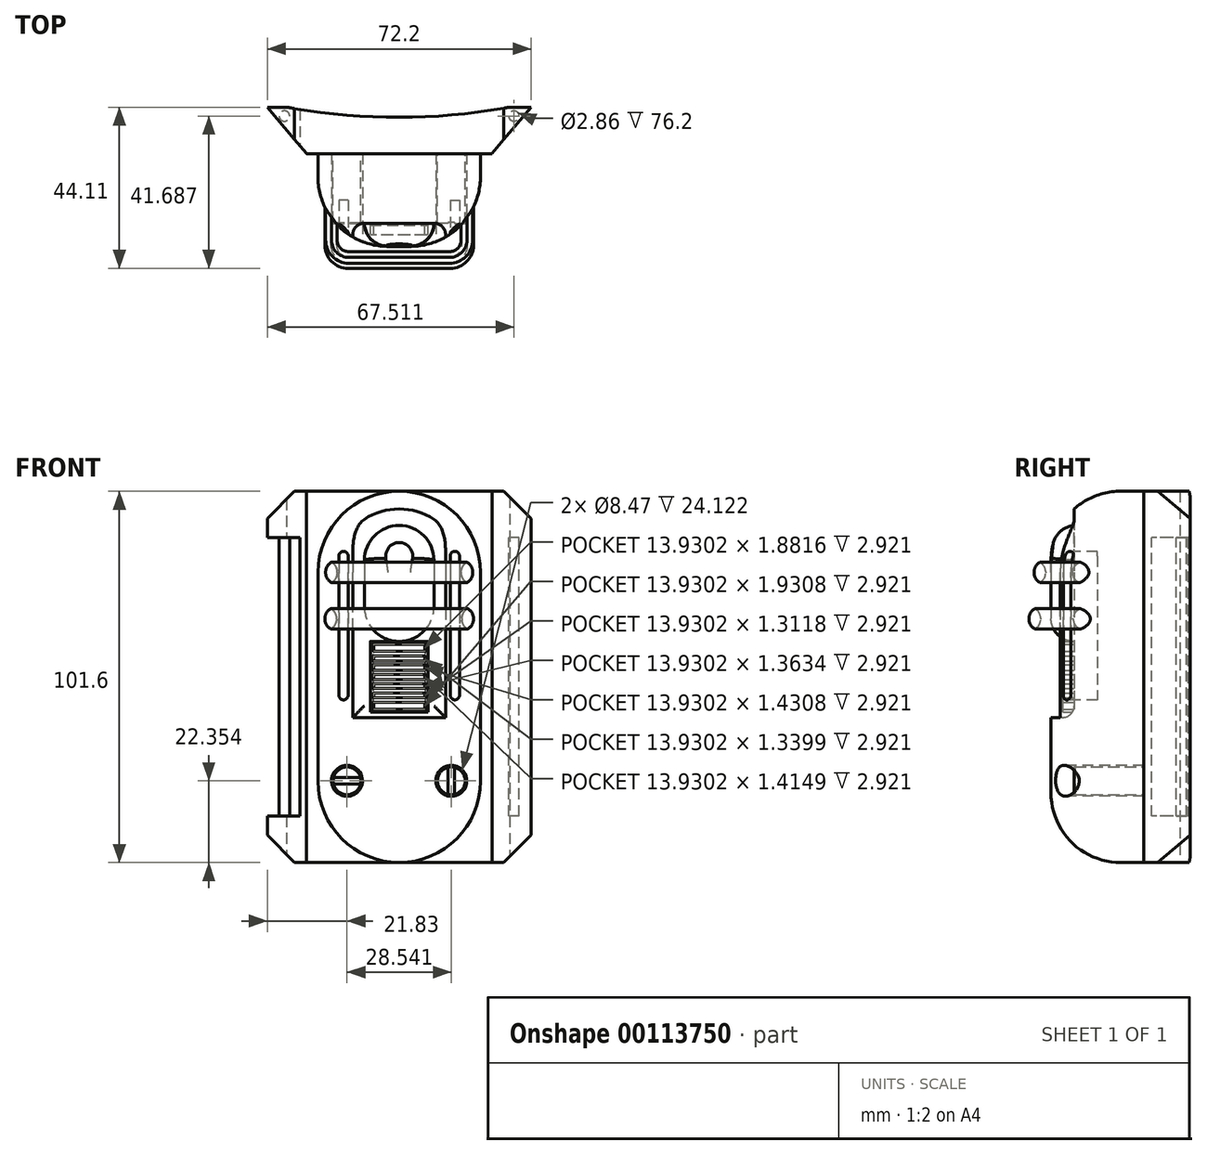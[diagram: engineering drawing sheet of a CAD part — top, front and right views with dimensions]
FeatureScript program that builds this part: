
annotation { "Feature Type Name" : "Feature", "Feature Type Description" : "" }
export const myFeature = defineFeature(function(context is Context, id is Id, definition is map)
    precondition{}
    {
        {
            var Q0;
            Q0=qCreatedBy(makeId("Front.planeOp"),FACE);
            var sketch = newSketch(context, id + "F0", { "sketchPlane" : qUnion([Q0])});
            skLineSegment(sketch, "E0.bottom", {"start": v(25.4, 50.8) * mm, "end": v(-25.4, 50.8) * mm});
            skLineSegment(sketch, "E0.top", {"start": v(25.4, -50.8) * mm, "end": v(-25.4, -50.8) * mm});
            skLineSegment(sketch, "E0.left", {"start": v(25.4, 50.8) * mm, "end": v(25.4, -50.8) * mm});
            skLineSegment(sketch, "E0.right", {"start": v(-25.4, 50.8) * mm, "end": v(-25.4, -50.8) * mm});
            skPoint(sketch, "E0.middle", {"position": v(0, 0) * mm});
            skSolve(sketch);
        }
        {
            var Q0;
            Q0 = qSketchRegion(id + "F0", true);
            extrude(context, id + "F1", {"entities" : qUnion([Q0]), "depth" : 12.7 * mm});
        }
        {
            var Q0;
            Q0=qCreatedBy(makeId("Top.planeOp"),FACE);
            var sketch = newSketch(context, id + "F2", { "sketchPlane" : qUnion([Q0])});
            skLineSegment(sketch, "E1", {"start": v(25.4, 0) * mm, "end": v(36.1, 0) * mm});
            skLineSegment(sketch, "E2", {"start": v(36.1, 0) * mm, "end": v(25.4, -12.67) * mm});
            skLineSegment(sketch, "E3", {"start": v(25.4, -12.67) * mm, "end": v(25.4, 0) * mm});
            skLineSegment(sketch, "E4.MirrorCS", {"start": v(-36.1, 0) * mm, "end": v(-25.4, -12.67) * mm});
            skLineSegment(sketch, "E5.MirrorCS", {"start": v(-25.4, -12.67) * mm, "end": v(-25.4, 0) * mm});
            skLineSegment(sketch, "E6.MirrorCS", {"start": v(-25.4, 0) * mm, "end": v(-36.1, 0) * mm});
            skSolve(sketch);
        }
        {
            var Q0;
            Q0 = qSketchRegion(id + "F2", true);
            extrude(context, id + "F3", {"entities" : qUnion([Q0]), "operationType" : NewBodyOperationType.ADD, "depth" : 101.6 * mm, "symmetric" : true});
        }
        {
            var Q0;
            Q0=qCreatedBy(makeId("Top.planeOp"),FACE);
            var sketch = newSketch(context, id + "F4", { "sketchPlane" : qUnion([Q0])});
            skCircle(sketch, "E7", {"center": v(-31.41, -2.42) * mm, "radius": 1.43 * mm});
            skCircle(sketch, "E8.MirrorC", {"center": v(31.41, -2.42) * mm, "radius": 1.43 * mm});
            skLineSegment(sketch, "E9.bottom", {"start": v(27.18, 1.43) * mm, "end": v(39.9, 1.43) * mm});
            skLineSegment(sketch, "E9.top", {"start": v(27.18, -11.19) * mm, "end": v(39.9, -11.19) * mm});
            skLineSegment(sketch, "E9.left", {"start": v(27.18, 1.43) * mm, "end": v(27.18, -11.19) * mm});
            skLineSegment(sketch, "E9.right", {"start": v(39.9, 1.43) * mm, "end": v(39.9, -11.19) * mm});
            skLineSegment(sketch, "E10.MirrorCS", {"start": v(-27.18, -11.19) * mm, "end": v(-39.9, -11.19) * mm});
            skLineSegment(sketch, "E11.MirrorCS", {"start": v(-39.9, 1.43) * mm, "end": v(-39.9, -11.19) * mm});
            skLineSegment(sketch, "E12.MirrorCS", {"start": v(-27.18, 1.43) * mm, "end": v(-39.9, 1.43) * mm});
            skLineSegment(sketch, "E13.MirrorCS", {"start": v(-27.18, 1.43) * mm, "end": v(-27.18, -11.19) * mm});
            skSolve(sketch);
        }
        {
            var Q0;
            Q0=makeQuery(id+"F4.imprint","IMPRINT",FACE,{"disambiguationData":[TD([[makeQuery(id+"F4.imprint","IMPRINT",EDGE,{"derivedFrom":sQuery(id+"F4.wireOp",EDGE,"E8.MirrorC")}),1.0]])]});
            var Q1;
            Q1=makeQuery(id+"F4.imprint","IMPRINT",FACE,{"disambiguationData":[TD([[makeQuery(id+"F4.imprint","IMPRINT",EDGE,{"derivedFrom":sQuery(id+"F4.wireOp",EDGE,"E7")}),-1.0]])]});
            extrude(context, id + "F5", {"entities" : qUnion([Q0, Q1]), "operationType" : NewBodyOperationType.REMOVE, "oppositeDirection" : true, "depth" : 76.2 * mm, "symmetric" : true});
        }
        {
            var Q0;
            Q0=qCreatedBy(makeId("Front.planeOp"),FACE);
            var sketch = newSketch(context, id + "F6", { "sketchPlane" : qUnion([Q0])});
            skLineSegment(sketch, "E14", {"start": v(-40.53, 38.9) * mm, "end": v(-23.28, 56.16) * mm});
            skLineSegment(sketch, "E15", {"start": v(-23.28, 56.16) * mm, "end": v(-40.53, 56.16) * mm});
            skLineSegment(sketch, "E16", {"start": v(-40.53, 56.16) * mm, "end": v(-40.53, 38.9) * mm});
            skLineSegment(sketch, "E17.MirrorCS", {"start": v(40.53, 56.16) * mm, "end": v(40.53, 38.9) * mm});
            skLineSegment(sketch, "E18.MirrorCS", {"start": v(23.28, 56.16) * mm, "end": v(40.53, 56.16) * mm});
            skLineSegment(sketch, "E19.MirrorCS", {"start": v(40.53, 38.9) * mm, "end": v(23.28, 56.16) * mm});
            skLineSegment(sketch, "E20.MirrorCS", {"start": v(-40.53, -56.16) * mm, "end": v(-40.53, -38.9) * mm});
            skLineSegment(sketch, "E21.MirrorCS", {"start": v(-23.28, -56.16) * mm, "end": v(-40.53, -56.16) * mm});
            skLineSegment(sketch, "E22.MirrorCS", {"start": v(-40.53, -38.9) * mm, "end": v(-23.28, -56.16) * mm});
            skLineSegment(sketch, "E23.MirrorCS", {"start": v(40.53, -38.9) * mm, "end": v(23.28, -56.16) * mm});
            skLineSegment(sketch, "E24.MirrorCS", {"start": v(23.28, -56.16) * mm, "end": v(40.53, -56.16) * mm});
            skLineSegment(sketch, "E25.MirrorCS", {"start": v(40.53, -56.16) * mm, "end": v(40.53, -38.9) * mm});
            skSolve(sketch);
        }
        {
            var Q0;
            Q0=makeQuery(id+"F6.imprint","IMPRINT",FACE,{"disambiguationData":[TD([[makeQuery(id+"F6.imprint","IMPRINT",EDGE,{"derivedFrom":sQuery(id+"F6.wireOp",EDGE,"E17.MirrorCS")}),-1.0]])]});
            var Q1;
            Q1=makeQuery(id+"F6.imprint","IMPRINT",FACE,{"disambiguationData":[TD([[makeQuery(id+"F6.imprint","IMPRINT",EDGE,{"derivedFrom":sQuery(id+"F6.wireOp",EDGE,"E20.MirrorCS")}),-1.0]])]});
            var Q2;
            Q2=makeQuery(id+"F6.imprint","IMPRINT",FACE,{"disambiguationData":[TD([[makeQuery(id+"F6.imprint","IMPRINT",EDGE,{"derivedFrom":sQuery(id+"F6.wireOp",EDGE,"E23.MirrorCS")}),1.0]])]});
            var Q3;
            Q3=makeQuery(id+"F6.imprint","IMPRINT",FACE,{"disambiguationData":[TD([[makeQuery(id+"F6.imprint","IMPRINT",EDGE,{"derivedFrom":sQuery(id+"F6.wireOp",EDGE,"E14")}),1.0]])]});
            extrude(context, id + "F7", {"entities" : qUnion([Q0, Q1, Q2, Q3]), "operationType" : NewBodyOperationType.REMOVE, "endBound" : BoundingType.THROUGH_ALL, "depth" : 25.4 * mm});
        }
        {
            var Q0;
            Q0=makeQuery(id+"F1.opExtrude","CAP_FACE",FACE,{"disambiguationData":[OSD([sQuery(id+"F0.wireOp",EDGE,"E0.bottom"),sQuery(id+"F0.wireOp",EDGE,"E0.top"),sQuery(id+"F0.wireOp",EDGE,"E0.left"),sQuery(id+"F0.wireOp",EDGE,"E0.right")])],"isStart":false});
            var sketch = newSketch(context, id + "F8", { "sketchPlane" : qUnion([Q0])});
            skLineSegment(sketch, "E26.bottom", {"start": v(22.23, 28.57) * mm, "end": v(-22.22, 28.57) * mm});
            skLineSegment(sketch, "E26.top", {"start": v(22.22, -28.58) * mm, "end": v(-22.22, -28.58) * mm});
            skLineSegment(sketch, "E26.left", {"start": v(22.22, 28.57) * mm, "end": v(22.22, -28.58) * mm});
            skLineSegment(sketch, "E26.right", {"start": v(-22.23, 28.57) * mm, "end": v(-22.23, -28.58) * mm});
            skPoint(sketch, "E26.middle", {"position": v(0, 0) * mm});
            skArc(sketch, "E27", {"start": v(22.23, 28.58) * mm, "mid": v(0, 50.8) * mm, "end": v(-22.23, 28.57) * mm});
            skArc(sketch, "E28", {"start": v(-22.23, -28.58) * mm, "mid": v(0, -50.8) * mm, "end": v(22.23, -28.58) * mm});
            skSolve(sketch);
        }
        {
            var Q0;
            Q0 = qSketchRegion(id + "F8", true);
            extrude(context, id + "F9", {"entities" : qUnion([Q0]), "operationType" : NewBodyOperationType.ADD, "depth" : 25.4 * mm});
        }
        {
            var Q0;
            Q0=makeQuery(id+"F9.opExtrude","CAP_EDGE",EDGE,{"disambiguationData":[OSD([sQuery(id+"F8.wireOp",EDGE,"E26.left")])],"isStart":false});
            fillet(context, id + "F10", {"entities" : qUnion([Q0]), "radius" : 19.05 * mm, "tangentPropagation" : true, "allowEdgeOverflow" : false});
        }
        {
            var Q0;
            Q0=makeQuery(id+"F9.opExtrude","CAP_FACE",FACE,{"disambiguationData":[OSD([sQuery(id+"F8.wireOp",EDGE,"E26.left"),sQuery(id+"F8.wireOp",EDGE,"E26.right"),sQuery(id+"F8.wireOp",EDGE,"E27"),sQuery(id+"F8.wireOp",EDGE,"E28")])],"isStart":false});
            var sketch = newSketch(context, id + "F11", { "sketchPlane" : qUnion([Q0])});
            skLineSegment(sketch, "E29.left", {"start": v(12.7, 103.58) * mm, "end": v(12.7, 7.15) * mm});
            skLineSegment(sketch, "E29.right", {"start": v(-12.7, 103.58) * mm, "end": v(-12.7, 7.15) * mm});
            skPoint(sketch, "E30.middle", {"position": v(0, 31.75) * mm});
            skLineSegment(sketch, "E31", {"start": v(-12.7, 103.58) * mm, "end": v(12.7, 103.58) * mm});
            skPoint(sketch, "E32.orphan", {"position": v(-12.7, 56.35) * mm});
            skPoint(sketch, "E33.orphan", {"position": v(12.7, 56.35) * mm});
            skLineSegment(sketch, "E34.bottom", {"start": v(9.52, 31.92) * mm, "end": v(-9.52, 31.92) * mm});
            skLineSegment(sketch, "E34.top", {"start": v(9.52, 19.22) * mm, "end": v(-9.52, 19.22) * mm});
            skLineSegment(sketch, "E34.left", {"start": v(9.52, 31.92) * mm, "end": v(9.52, 19.22) * mm});
            skLineSegment(sketch, "E34.right", {"start": v(-9.52, 31.92) * mm, "end": v(-9.52, 19.22) * mm});
            skPoint(sketch, "E34.middle", {"position": v(0, 25.57) * mm});
            skArc(sketch, "E35", {"start": v(-9.52, 19.22) * mm, "mid": v(0, 9.7) * mm, "end": v(9.52, 19.22) * mm});
            skArc(sketch, "E36", {"start": v(9.52, 31.92) * mm, "mid": v(0, 41.44) * mm, "end": v(-9.52, 31.92) * mm});
            skLineSegment(sketch, "E37.top", {"start": v(-12.7, -11.11) * mm, "end": v(12.7, -11.11) * mm});
            skLineSegment(sketch, "E37.left", {"start": v(-12.7, 7.15) * mm, "end": v(-12.7, -11.11) * mm});
            skLineSegment(sketch, "E37.right", {"start": v(12.7, 7.15) * mm, "end": v(12.7, -11.11) * mm});
            skSolve(sketch);
        }
        {
            var Q0;
            Q0 = qSketchRegion(id + "F11", true);
            extrude(context, id + "F12", {"entities" : qUnion([Q0]), "operationType" : NewBodyOperationType.REMOVE, "oppositeDirection" : true, "depth" : 6.35 * mm});
        }
        {
            var Q0;
            Q0=makeQuery(id+"F12.boolean.opBoolean","INTERSECT",EDGE,{"derivedFrom":[makeQuery(id+"F10.opFillet","BLEND_FACE",FACE,{"disambiguationData":[OSD([sQuery(id+"F8.wireOp",EDGE,"E26.right")])]}),makeQuery(id+"F12.opExtrude","SWEPT_FACE",FACE,{"disambiguationData":[OSD([sQuery(id+"F11.wireOp",EDGE,"E34.right")])]})]});
            fillet(context, id + "F13", {"entities" : qUnion([Q0]), "radius" : 6.35 * mm, "tangentPropagation" : true, "allowEdgeOverflow" : false});
        }
        {
            var Q0;
            {var subQ0=sQuery(id+"F8.wireOp",EDGE,"E26.left");var subQ1=sQuery(id+"F8.wireOp",EDGE,"E26.right");var subQ2=sQuery(id+"F8.wireOp",EDGE,"E28");Q0=makeQuery(id+"F12.boolean.opBoolean","SPLIT",FACE,{"disambiguationData":[TD([makeQuery(id+"F10.opFillet","BLEND_FACE",FACE,{"disambiguationData":[OSD([subQ2])]})])],"derivedFrom":makeQuery(id+"F9.opExtrude","CAP_FACE",FACE,{"disambiguationData":[OSD([subQ0,subQ1,sQuery(id+"F8.wireOp",EDGE,"E27"),subQ2])],"isStart":false})});}
            var sketch = newSketch(context, id + "F14", { "sketchPlane" : qUnion([Q0])});
            skCircle(sketch, "E38", {"center": v(-14.27, -28.45) * mm, "radius": 4.23 * mm});
            skCircle(sketch, "E39.MirrorC", {"center": v(14.27, -28.45) * mm, "radius": 4.23 * mm});
            skSolve(sketch);
        }
        {
            var Q0;
            Q0 = qSketchRegion(id + "F14", true);
            extrude(context, id + "F15", {"entities" : qUnion([Q0]), "operationType" : NewBodyOperationType.REMOVE, "oppositeDirection" : true, "depth" : 25.4 * mm});
        }
        {
            var Q0;
            Q0=makeQuery(id+"F15.boolean.opBoolean","COPY",FACE,{"derivedFrom":makeQuery(id+"F15.opExtrude","CAP_FACE",FACE,{"disambiguationData":[OSD([sQuery(id+"F14.wireOp",EDGE,"E38")])],"isStart":false})});
            var sketch = newSketch(context, id + "F16", { "sketchPlane" : qUnion([Q0])});
            skCircle(sketch, "E40", {"center": v(-14.27, -28.45) * mm, "radius": 3.81 * mm});
            skCircle(sketch, "E41.MirrorC", {"center": v(14.27, -28.45) * mm, "radius": 3.81 * mm});
            skSolve(sketch);
        }
        {
            var Q0;
            Q0 = qSketchRegion(id + "F16", true);
            extrude(context, id + "F17", {"entities" : qUnion([Q0]), "operationType" : NewBodyOperationType.ADD, "depth" : 19.05 * mm});
        }
        {
            var Q0;
            Q0=makeQuery(id+"F17.opExtrude","CAP_FACE",FACE,{"disambiguationData":[OSD([sQuery(id+"F16.wireOp",EDGE,"E40")])],"isStart":false});
            var sketch = newSketch(context, id + "F18", { "sketchPlane" : qUnion([Q0])});
            skLineSegment(sketch, "E42.bottom", {"start": v(-17.97, -29.34) * mm, "end": v(-10.56, -29.34) * mm});
            skLineSegment(sketch, "E42.top", {"start": v(-17.98, -27.57) * mm, "end": v(-10.56, -27.57) * mm});
            skLineSegment(sketch, "E42.right", {"start": v(-10.56, -29.34) * mm, "end": v(-10.56, -29.32) * mm});
            skArc(sketch, "E43.0", {"start": v(-10.57, -29.34) * mm, "mid": v(-10.46, -28.46) * mm, "end": v(-10.56, -27.57) * mm});
            skArc(sketch, "E44.trimOffspring", {"start": v(-17.98, -27.57) * mm, "mid": v(-18.08, -28.46) * mm, "end": v(-17.97, -29.34) * mm});
            skArc(sketch, "E45.0", {"start": v(15.15, -24.74) * mm, "mid": v(14.27, -24.64) * mm, "end": v(13.4, -24.74) * mm});
            skLineSegment(sketch, "E46.left", {"start": v(15.15, -24.74) * mm, "end": v(15.15, -32.15) * mm});
            skLineSegment(sketch, "E46.right", {"start": v(13.4, -24.74) * mm, "end": v(13.4, -32.15) * mm});
            skArc(sketch, "E47.trimOffspring", {"start": v(13.4, -32.15) * mm, "mid": v(14.27, -32.26) * mm, "end": v(15.15, -32.15) * mm});
            skSolve(sketch);
        }
        {
            var Q0;
            Q0 = qSketchRegion(id + "F18", true);
            extrude(context, id + "F19", {"entities" : qUnion([Q0]), "operationType" : NewBodyOperationType.REMOVE, "oppositeDirection" : true, "depth" : 0.25 * mm});
        }
        {
            var Q0;
            {var subQ0=sQuery(id+"F8.wireOp",EDGE,"E26.left");var subQ1=sQuery(id+"F8.wireOp",EDGE,"E26.right");var subQ2=sQuery(id+"F8.wireOp",EDGE,"E28");Q0=makeQuery(id+"F12.boolean.opBoolean","SPLIT",FACE,{"disambiguationData":[TD([makeQuery(id+"F10.opFillet","BLEND_FACE",FACE,{"disambiguationData":[OSD([subQ2])]})])],"derivedFrom":makeQuery(id+"F9.opExtrude","CAP_FACE",FACE,{"disambiguationData":[OSD([subQ0,subQ1,sQuery(id+"F8.wireOp",EDGE,"E27"),subQ2])],"isStart":false})});}
            var sketch = newSketch(context, id + "F20", { "sketchPlane" : qUnion([Q0])});
            skLineSegment(sketch, "E48.left", {"start": v(-16.5, 33.08) * mm, "end": v(-16.5, -5.02) * mm});
            skLineSegment(sketch, "E48.right", {"start": v(-13.97, 33.08) * mm, "end": v(-13.97, -5.02) * mm});
            skArc(sketch, "E49", {"start": v(-13.97, 33.08) * mm, "mid": v(-15.24, 34.35) * mm, "end": v(-16.5, 33.08) * mm});
            skArc(sketch, "E50", {"start": v(-16.5, -5.02) * mm, "mid": v(-15.24, -6.3) * mm, "end": v(-13.97, -5.02) * mm});
            skLineSegment(sketch, "E51.MirrorCS", {"start": v(16.5, 33.08) * mm, "end": v(16.5, -5.02) * mm});
            skLineSegment(sketch, "E52.MirrorCS", {"start": v(13.97, 33.08) * mm, "end": v(13.97, -5.02) * mm});
            skArc(sketch, "E53.MirrorCS", {"start": v(16.5, -5.02) * mm, "mid": v(15.24, -6.3) * mm, "end": v(13.97, -5.02) * mm});
            skArc(sketch, "E54.MirrorCS", {"start": v(13.97, 33.08) * mm, "mid": v(15.24, 34.35) * mm, "end": v(16.5, 33.08) * mm});
            skSolve(sketch);
        }
        {
            var Q0;
            Q0 = qSketchRegion(id + "F20", true);
            extrude(context, id + "F21", {"entities" : qUnion([Q0]), "operationType" : NewBodyOperationType.REMOVE, "oppositeDirection" : true, "depth" : 12.7 * mm});
        }
        {
            var Q0;
            Q0=qCreatedBy(makeId("Top.planeOp"),FACE);
            cPlane(context, id + "F22", {"entities" : qUnion([Q0]), "cplaneType" : CPlaneType.OFFSET, "offset" : 28.57 * mm, "width" : 152.4 * mm, "height" : 152.4 * mm});
        }
        {
            var Q0;
            Q0=qCreatedBy(id+"F22.planeOp",FACE);
            var sketch = newSketch(context, id + "F23", { "sketchPlane" : qUnion([Q0])});
            skLineSegment(sketch, "E55.bottom", {"start": v(0, -42.73) * mm, "end": v(-13.78, -42.73) * mm});
            skLineSegment(sketch, "E55.right", {"start": v(-20.13, -36.38) * mm, "end": v(-20.13, -27.04) * mm});
            skPoint(sketch, "E55.middle", {"position": v(-1.1, -33.3) * mm});
            skLineSegment(sketch, "E56.bottom", {"start": v(0, -39.56) * mm, "end": v(-13.78, -39.56) * mm});
            skLineSegment(sketch, "E56.right", {"start": v(-16.95, -36.38) * mm, "end": v(-16.95, -27.04) * mm});
            skPoint(sketch, "E57.orphan", {"position": v(14.74, -27.04) * mm});
            skPoint(sketch, "E58.orphan", {"position": v(17.92, -23.87) * mm});
            skLineSegment(sketch, "E59.trimOffspring", {"start": v(-16.95, -27.04) * mm, "end": v(-20.13, -27.04) * mm});
            skPoint(sketch, "E60.orphan", {"position": v(-20.13, -23.87) * mm});
            skPoint(sketch, "E61.visualSharp", {"position": v(-20.13, -42.73) * mm});
            skArc(sketch, "E61.filletArc", {"start": v(-20.13, -36.38) * mm, "mid": v(-18.27, -40.87) * mm, "end": v(-13.78, -42.73) * mm});
            skPoint(sketch, "E62.visualSharp", {"position": v(-16.95, -39.56) * mm});
            skArc(sketch, "E62.filletArc", {"start": v(-16.95, -36.38) * mm, "mid": v(-16.02, -38.63) * mm, "end": v(-13.78, -39.56) * mm});
            skPoint(sketch, "E63.visualSharp", {"position": v(14.74, -39.56) * mm});
            skPoint(sketch, "E64.visualSharp", {"position": v(17.92, -42.73) * mm});
            skLineSegment(sketch, "E65.MirrorCS", {"start": v(0, -42.73) * mm, "end": v(13.78, -42.73) * mm});
            skLineSegment(sketch, "E66.MirrorCS", {"start": v(0, -39.56) * mm, "end": v(13.78, -39.56) * mm});
            skArc(sketch, "E67.MirrorCS", {"start": v(20.13, -36.38) * mm, "mid": v(18.27, -40.87) * mm, "end": v(13.78, -42.73) * mm});
            skArc(sketch, "E68.MirrorCS", {"start": v(16.95, -36.38) * mm, "mid": v(16.02, -38.63) * mm, "end": v(13.78, -39.56) * mm});
            skLineSegment(sketch, "E69.MirrorCS", {"start": v(16.95, -36.38) * mm, "end": v(16.95, -27.04) * mm});
            skLineSegment(sketch, "E70.MirrorCS", {"start": v(20.13, -36.38) * mm, "end": v(20.13, -27.04) * mm});
            skLineSegment(sketch, "E71.MirrorCS", {"start": v(16.95, -27.04) * mm, "end": v(20.13, -27.04) * mm});
            skSolve(sketch);
        }
        {
            var Q0;
            Q0=qCreatedBy(id+"F22.planeOp",FACE);
            cPlane(context, id + "F24", {"entities" : qUnion([Q0]), "cplaneType" : CPlaneType.OFFSET, "offset" : 12.7 * mm, "oppositeDirection" : true, "width" : 152.4 * mm, "height" : 152.4 * mm});
        }
        {
            var Q0;
            Q0=qCreatedBy(id+"F24.planeOp",FACE);
            var sketch = newSketch(context, id + "F25", { "sketchPlane" : qUnion([Q0])});
            skLineSegment(sketch, "E72.bottom", {"start": v(13.97, -44.11) * mm, "end": v(-13.97, -44.11) * mm});
            skLineSegment(sketch, "E72.left", {"start": v(20.32, -37.76) * mm, "end": v(20.32, -27.06) * mm});
            skLineSegment(sketch, "E72.right", {"start": v(-20.32, -37.76) * mm, "end": v(-20.32, -27.06) * mm});
            skPoint(sketch, "E72.middle", {"position": v(0, -34) * mm});
            skLineSegment(sketch, "E73.bottom", {"start": v(13.97, -40.94) * mm, "end": v(-13.97, -40.94) * mm});
            skLineSegment(sketch, "E73.top", {"start": v(20.32, -27.06) * mm, "end": v(15.84, -27.06) * mm});
            skLineSegment(sketch, "E73.left", {"start": v(17.15, -37.76) * mm, "end": v(17.15, -27.06) * mm});
            skLineSegment(sketch, "E73.right", {"start": v(-17.15, -37.76) * mm, "end": v(-17.15, -27.06) * mm});
            skPoint(sketch, "E74.orphan", {"position": v(17.15, -27.06) * mm});
            skPoint(sketch, "E75.orphan", {"position": v(20.32, -23.88) * mm});
            skLineSegment(sketch, "E76.trimOffspring", {"start": v(-17.15, -27.06) * mm, "end": v(-20.32, -27.06) * mm});
            skPoint(sketch, "E77.orphan", {"position": v(-20.32, -23.88) * mm});
            skPoint(sketch, "E78.visualSharp", {"position": v(-20.32, -44.11) * mm});
            skArc(sketch, "E78.filletArc", {"start": v(-20.32, -37.76) * mm, "mid": v(-18.46, -42.25) * mm, "end": v(-13.97, -44.11) * mm});
            skPoint(sketch, "E79.visualSharp", {"position": v(-17.15, -40.94) * mm});
            skArc(sketch, "E79.filletArc", {"start": v(-17.15, -37.76) * mm, "mid": v(-16.22, -40) * mm, "end": v(-13.97, -40.94) * mm});
            skPoint(sketch, "E80.visualSharp", {"position": v(17.15, -40.94) * mm});
            skArc(sketch, "E80.filletArc", {"start": v(13.97, -40.94) * mm, "mid": v(16.22, -40) * mm, "end": v(17.15, -37.76) * mm});
            skPoint(sketch, "E81.visualSharp", {"position": v(20.32, -44.11) * mm});
            skArc(sketch, "E81.filletArc", {"start": v(13.97, -44.11) * mm, "mid": v(18.46, -42.25) * mm, "end": v(20.32, -37.76) * mm});
            skSolve(sketch);
        }
        {
            var Q0;
            Q0 = qSketchRegion(id + "F23", true);
            extrude(context, id + "F26", {"entities" : qUnion([Q0]), "operationType" : NewBodyOperationType.ADD, "depth" : 6.35 * mm, "symmetric" : true});
        }
        {
            var Q0;
            Q0=makeQuery(id+"F26.opExtrude","CAP_EDGE",EDGE,{"disambiguationData":[OSD([sQuery(id+"F23.wireOp",EDGE,"E55.bottom")])],"isStart":true});
            var Q1;
            Q1=makeQuery(id+"F26.opExtrude","CAP_EDGE",EDGE,{"disambiguationData":[OSD([sQuery(id+"F23.wireOp",EDGE,"E55.bottom")])],"isStart":false});
            var Q2;
            Q2=makeQuery(id+"F26.opExtrude","CAP_EDGE",EDGE,{"disambiguationData":[OSD([sQuery(id+"F23.wireOp",EDGE,"E56.bottom")])],"isStart":true});
            var Q3;
            Q3=makeQuery(id+"F26.opExtrude","CAP_EDGE",EDGE,{"disambiguationData":[OSD([sQuery(id+"F23.wireOp",EDGE,"E56.bottom")])],"isStart":false});
            fillet(context, id + "F27", {"entities" : qUnion([Q0, Q1, Q2, Q3]), "radius" : 3.05 * mm, "tangentPropagation" : true, "allowEdgeOverflow" : false});
        }
        {
            var Q0;
            Q0 = qSketchRegion(id + "F25", true);
            extrude(context, id + "F28", {"entities" : qUnion([Q0]), "operationType" : NewBodyOperationType.ADD, "depth" : 6.35 * mm, "symmetric" : true});
        }
        {
            var Q0;
            Q0=makeQuery(id+"F28.opExtrude","CAP_EDGE",EDGE,{"disambiguationData":[OSD([sQuery(id+"F25.wireOp",EDGE,"E72.bottom")])],"isStart":false});
            var Q1;
            Q1=makeQuery(id+"F28.opExtrude","CAP_EDGE",EDGE,{"disambiguationData":[OSD([sQuery(id+"F25.wireOp",EDGE,"E73.bottom")])],"isStart":false});
            var Q2;
            Q2=makeQuery(id+"F28.opExtrude","CAP_EDGE",EDGE,{"disambiguationData":[OSD([sQuery(id+"F25.wireOp",EDGE,"E72.bottom")])],"isStart":true});
            var Q3;
            Q3=makeQuery(id+"F28.opExtrude","CAP_EDGE",EDGE,{"disambiguationData":[OSD([sQuery(id+"F25.wireOp",EDGE,"E73.bottom")])],"isStart":true});
            fillet(context, id + "F29", {"entities" : qUnion([Q0, Q1, Q2, Q3]), "radius" : 3.05 * mm, "tangentPropagation" : true, "allowEdgeOverflow" : false});
        }
        {
            var Q0;
            Q0=makeQuery(id+"F12.boolean.opBoolean","COPY",FACE,{"derivedFrom":makeQuery(id+"F12.opExtrude","CAP_FACE",FACE,{"disambiguationData":[OSD([sQuery(id+"F11.wireOp",EDGE,"E29.left"),sQuery(id+"F11.wireOp",EDGE,"E29.right"),sQuery(id+"F11.wireOp",EDGE,"E31"),sQuery(id+"F11.wireOp",EDGE,"E34.left"),sQuery(id+"F11.wireOp",EDGE,"E34.right"),sQuery(id+"F11.wireOp",EDGE,"E35"),sQuery(id+"F11.wireOp",EDGE,"E36"),sQuery(id+"F11.wireOp",EDGE,"E37.top"),sQuery(id+"F11.wireOp",EDGE,"E37.left"),sQuery(id+"F11.wireOp",EDGE,"E37.right")])],"isStart":false})});
            var sketch = newSketch(context, id + "F30", { "sketchPlane" : qUnion([Q0])});
            skLineSegment(sketch, "E82.bottom", {"start": v(6.97, 8.9) * mm, "end": v(-6.97, 8.9) * mm});
            skLineSegment(sketch, "E82.top", {"start": v(6.97, -8.9) * mm, "end": v(-6.97, -8.9) * mm});
            skLineSegment(sketch, "E82.left", {"start": v(6.97, 8.9) * mm, "end": v(6.97, 7) * mm});
            skLineSegment(sketch, "E82.right", {"start": v(-6.97, 8.9) * mm, "end": v(-6.97, 7) * mm});
            skPoint(sketch, "E82.middle", {"position": v(0, 0) * mm});
            skPoint(sketch, "E83.orphan", {"position": v(-6.97, 0) * mm});
            skPoint(sketch, "E84.start.orphan", {"position": v(6.97, 0) * mm});
            skLineSegment(sketch, "E85.bottom", {"start": v(7.88, 9.69) * mm, "end": v(-7.88, 9.69) * mm});
            skLineSegment(sketch, "E85.top", {"start": v(7.88, -9.69) * mm, "end": v(-7.88, -9.69) * mm});
            skLineSegment(sketch, "E85.left", {"start": v(7.88, 9.69) * mm, "end": v(7.88, -9.69) * mm});
            skLineSegment(sketch, "E85.right", {"start": v(-7.88, 9.69) * mm, "end": v(-7.88, -9.69) * mm});
            skLineSegment(sketch, "E86.bottom", {"start": v(6.97, 5.7) * mm, "end": v(-6.97, 5.7) * mm});
            skLineSegment(sketch, "E86.top", {"start": v(6.97, 7) * mm, "end": v(-6.97, 7) * mm});
            skPoint(sketch, "E86.middle", {"position": v(0, 6.35) * mm});
            skLineSegment(sketch, "E87.bottom", {"start": v(6.97, 3.27) * mm, "end": v(-6.97, 3.27) * mm});
            skLineSegment(sketch, "E87.top", {"start": v(6.97, 4.35) * mm, "end": v(-6.97, 4.35) * mm});
            skPoint(sketch, "E87.middle", {"position": v(0, 3.81) * mm});
            skLineSegment(sketch, "E88.bottom", {"start": v(6.97, 0.7) * mm, "end": v(-6.97, 0.7) * mm});
            skLineSegment(sketch, "E88.top", {"start": v(6.97, 1.84) * mm, "end": v(-6.97, 1.84) * mm});
            skPoint(sketch, "E88.middle", {"position": v(0, 1.27) * mm});
            skLineSegment(sketch, "E89.bottom", {"start": v(6.97, -1.83) * mm, "end": v(-6.97, -1.83) * mm});
            skLineSegment(sketch, "E89.top", {"start": v(6.97, -0.71) * mm, "end": v(-6.97, -0.71) * mm});
            skPoint(sketch, "E89.middle", {"position": v(0, -1.27) * mm});
            skLineSegment(sketch, "E90.bottom", {"start": v(6.97, -4.43) * mm, "end": v(-6.97, -4.43) * mm});
            skLineSegment(sketch, "E90.top", {"start": v(6.97, -3.2) * mm, "end": v(-6.97, -3.2) * mm});
            skPoint(sketch, "E90.middle", {"position": v(0, -3.81) * mm});
            skLineSegment(sketch, "E91.bottom", {"start": v(6.97, -6.96) * mm, "end": v(-6.97, -6.96) * mm});
            skLineSegment(sketch, "E91.top", {"start": v(6.97, -5.74) * mm, "end": v(-6.97, -5.74) * mm});
            skPoint(sketch, "E91.middle", {"position": v(0, -6.35) * mm});
            skLineSegment(sketch, "E92.trimOffspring", {"start": v(-6.97, 5.7) * mm, "end": v(-6.97, 4.35) * mm});
            skLineSegment(sketch, "E93.trimOffspring", {"start": v(-6.97, 3.27) * mm, "end": v(-6.97, 1.84) * mm});
            skLineSegment(sketch, "E94.trimOffspring", {"start": v(-6.97, 0.7) * mm, "end": v(-6.97, 0) * mm});
            skLineSegment(sketch, "E95.trimOffspring", {"start": v(-6.97, -1.83) * mm, "end": v(-6.97, -3.2) * mm});
            skLineSegment(sketch, "E96.trimOffspring", {"start": v(-6.97, -4.43) * mm, "end": v(-6.97, -5.74) * mm});
            skLineSegment(sketch, "E97.trimOffspring", {"start": v(-6.97, -6.96) * mm, "end": v(-6.97, -8.9) * mm});
            skLineSegment(sketch, "E98.trimOffspring", {"start": v(6.97, -6.96) * mm, "end": v(6.97, -8.9) * mm});
            skLineSegment(sketch, "E99.trimOffspring", {"start": v(6.97, -4.43) * mm, "end": v(6.97, -5.74) * mm});
            skLineSegment(sketch, "E100.trimOffspring", {"start": v(6.97, -1.83) * mm, "end": v(6.97, -3.2) * mm});
            skLineSegment(sketch, "E101.trimOffspring", {"start": v(6.97, 0.7) * mm, "end": v(6.97, -0.71) * mm});
            skLineSegment(sketch, "E102.trimOffspring", {"start": v(6.97, 3.27) * mm, "end": v(6.97, 1.84) * mm});
            skLineSegment(sketch, "E103.trimOffspring", {"start": v(6.97, 5.7) * mm, "end": v(6.97, 4.35) * mm});
            skLineSegment(sketch, "E104", {"start": v(-6.97, -0.71) * mm, "end": v(-6.97, 0) * mm});
            skSolve(sketch);
        }
        {
            var Q0;
            Q0 = qSketchRegion(id + "F30", true);
            extrude(context, id + "F31", {"entities" : qUnion([Q0]), "operationType" : NewBodyOperationType.ADD, "depth" : 3.17 * mm});
        }
        {
            var Q0;
            Q0=makeQuery(id+"F31.opExtrude","CAP_FACE",FACE,{"disambiguationData":[OSD([sQuery(id+"F30.wireOp",EDGE,"E82.bottom"),sQuery(id+"F30.wireOp",EDGE,"E82.top"),sQuery(id+"F30.wireOp",EDGE,"E82.left"),sQuery(id+"F30.wireOp",EDGE,"E82.right"),sQuery(id+"F30.wireOp",EDGE,"E85.bottom"),sQuery(id+"F30.wireOp",EDGE,"E85.top"),sQuery(id+"F30.wireOp",EDGE,"E85.left"),sQuery(id+"F30.wireOp",EDGE,"E85.right"),sQuery(id+"F30.wireOp",EDGE,"E86.bottom"),sQuery(id+"F30.wireOp",EDGE,"E86.top"),sQuery(id+"F30.wireOp",EDGE,"E87.bottom"),sQuery(id+"F30.wireOp",EDGE,"E87.top"),sQuery(id+"F30.wireOp",EDGE,"E88.bottom"),sQuery(id+"F30.wireOp",EDGE,"E88.top"),sQuery(id+"F30.wireOp",EDGE,"E89.bottom"),sQuery(id+"F30.wireOp",EDGE,"E89.top"),sQuery(id+"F30.wireOp",EDGE,"E90.bottom"),sQuery(id+"F30.wireOp",EDGE,"E90.top"),sQuery(id+"F30.wireOp",EDGE,"E91.bottom"),sQuery(id+"F30.wireOp",EDGE,"E91.top"),sQuery(id+"F30.wireOp",EDGE,"E92.trimOffspring"),sQuery(id+"F30.wireOp",EDGE,"E93.trimOffspring"),sQuery(id+"F30.wireOp",EDGE,"E94.trimOffspring"),sQuery(id+"F30.wireOp",EDGE,"E95.trimOffspring"),sQuery(id+"F30.wireOp",EDGE,"E96.trimOffspring"),sQuery(id+"F30.wireOp",EDGE,"E97.trimOffspring"),sQuery(id+"F30.wireOp",EDGE,"E98.trimOffspring"),sQuery(id+"F30.wireOp",EDGE,"E99.trimOffspring"),sQuery(id+"F30.wireOp",EDGE,"E100.trimOffspring"),sQuery(id+"F30.wireOp",EDGE,"E101.trimOffspring"),sQuery(id+"F30.wireOp",EDGE,"E102.trimOffspring"),sQuery(id+"F30.wireOp",EDGE,"E103.trimOffspring"),sQuery(id+"F30.wireOp",EDGE,"E104")])],"isStart":false});
            fillet(context, id + "F32", {"entities" : qUnion([Q0]), "radius" : 0.25 * mm, "tangentPropagation" : true, "allowEdgeOverflow" : false});
        }
        {
            var Q0;
            Q0=makeQuery(id+"F12.boolean.opBoolean","COPY",EDGE,{"derivedFrom":makeQuery(id+"F12.opExtrude","CAP_EDGE",EDGE,{"disambiguationData":[OSD([sQuery(id+"F11.wireOp",EDGE,"E29.left"),sQuery(id+"F11.wireOp",EDGE,"E37.right")])],"isStart":false})});
            var Q1;
            Q1=makeQuery(id+"F12.boolean.opBoolean","COPY",EDGE,{"derivedFrom":makeQuery(id+"F12.opExtrude","CAP_EDGE",EDGE,{"disambiguationData":[OSD([sQuery(id+"F11.wireOp",EDGE,"E29.right"),sQuery(id+"F11.wireOp",EDGE,"E37.left")])],"isStart":false})});
            var Q2;
            Q2=makeQuery(id+"F12.boolean.opBoolean","COPY",EDGE,{"derivedFrom":makeQuery(id+"F12.opExtrude","CAP_EDGE",EDGE,{"disambiguationData":[OSD([sQuery(id+"F11.wireOp",EDGE,"E37.top")])],"isStart":false})});
            fillet(context, id + "F33", {"entities" : qUnion([Q0, Q1, Q2]), "radius" : 3.17 * mm, "tangentPropagation" : true, "allowEdgeOverflow" : false});
        }
        {
            var Q0;
            Q0=qCreatedBy(makeId("Top.planeOp"),FACE);
            var sketch = newSketch(context, id + "F34", { "sketchPlane" : qUnion([Q0])});
            skCircle(sketch, "E105", {"center": v(-0.3, 165.55) * mm, "radius": 168.33 * mm});
            skPoint(sketch, "E105.first.point", {"position": v(-30.78, 0) * mm});
            skPoint(sketch, "E105.second.point", {"position": v(30.2, 0) * mm});
            skPoint(sketch, "E105.third.point", {"position": v(13.86, -2.19) * mm});
            skSolve(sketch);
        }
        {
            var Q0;
            Q0 = qSketchRegion(id + "F34", true);
            extrude(context, id + "F35", {"entities" : qUnion([Q0]), "operationType" : NewBodyOperationType.REMOVE, "depth" : 152.4 * mm, "symmetric" : true});
        }
        {
            var Q0;
            Q0=makeQuery(id+"F1.opExtrude","SWEPT_BODY",BODY,{"disambiguationData":[OSD([sQuery(id+"F0.wireOp",EDGE,"E0.bottom"),sQuery(id+"F0.wireOp",EDGE,"E0.top"),sQuery(id+"F0.wireOp",EDGE,"E0.left"),sQuery(id+"F0.wireOp",EDGE,"E0.right")])]});
            transform(context, id + "F36", {"entities" : qUnion([Q0]), "transformType" : TransformType.TRANSLATION_3D, "dx" : 0 * mm, "dy" : 0 * mm, "dz" : 0 * mm, "makeCopy" : true});
        }
        {
            var Q0;
            Q0=makeQuery(id+"F36.opPattern","COPY",BODY,{"derivedFrom":makeQuery(id+"F1.opExtrude","SWEPT_BODY",BODY,{"disambiguationData":[OSD([sQuery(id+"F0.wireOp",EDGE,"E0.bottom"),sQuery(id+"F0.wireOp",EDGE,"E0.top"),sQuery(id+"F0.wireOp",EDGE,"E0.left"),sQuery(id+"F0.wireOp",EDGE,"E0.right")])]}),"instanceName":"1"});
            deleteBodies(context, id + "F37", {"entities" : qUnion([Q0])});
        }
    });
